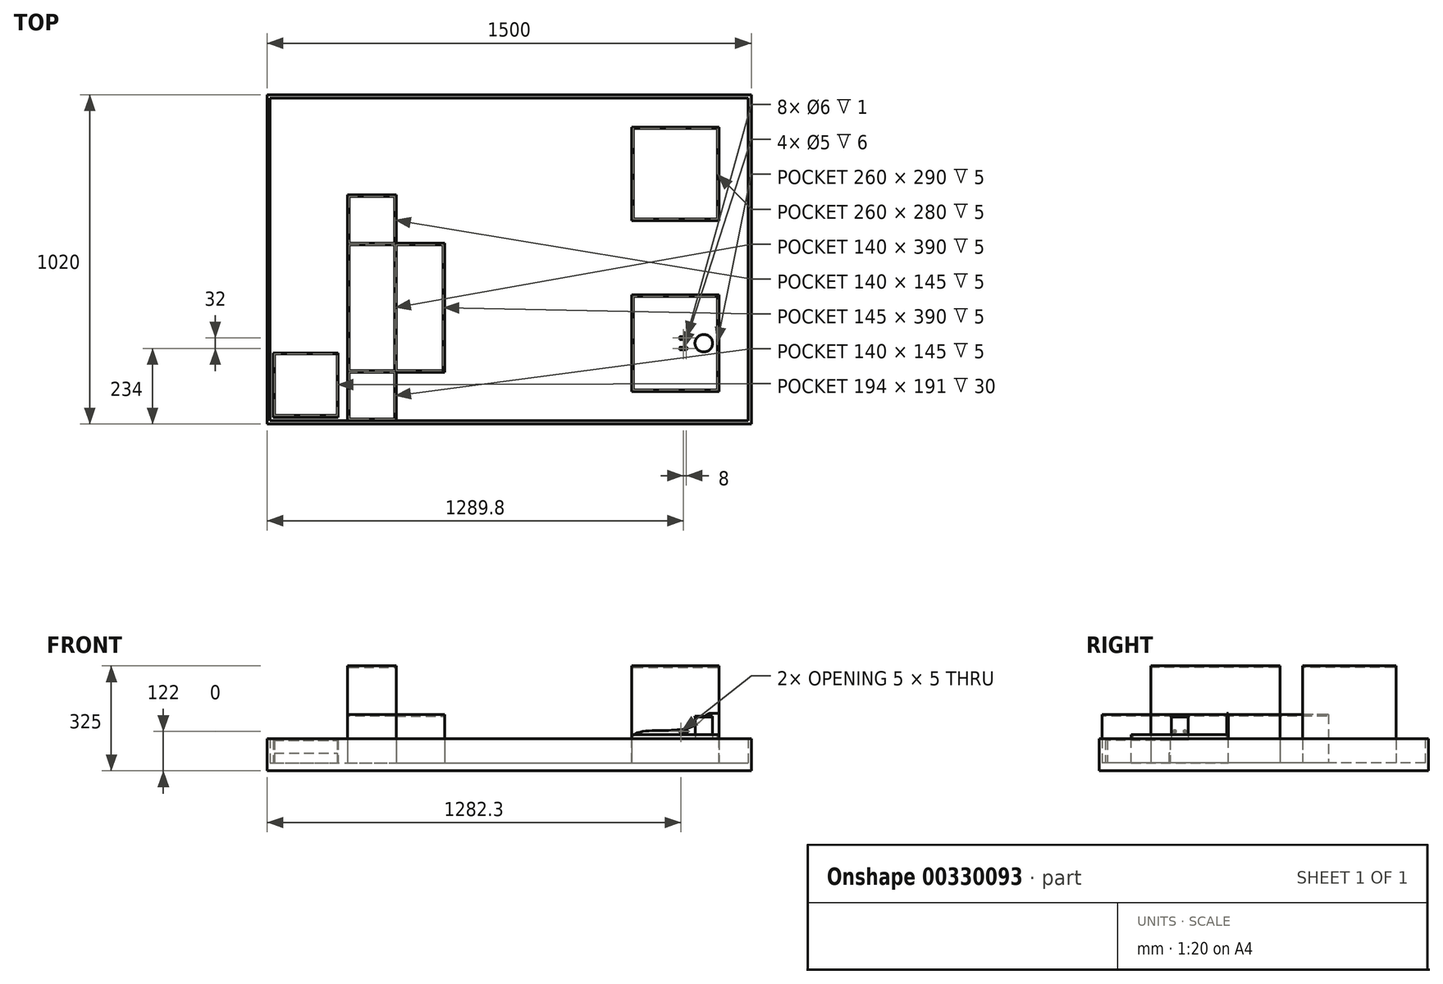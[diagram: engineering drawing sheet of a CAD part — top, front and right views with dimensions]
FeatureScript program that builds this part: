
annotation { "Feature Type Name" : "Feature", "Feature Type Description" : "" }
export const myFeature = defineFeature(function(context is Context, id is Id, definition is map)
    precondition{}
    {
        {
            var Q0;
            Q0=qCreatedBy(makeId("Top.planeOp"),FACE);
            var sketch = newSketch(context, id + "F0", { "sketchPlane" : qUnion([Q0])});
            skCircle(sketch, "E0", {"center": v(0, 0) * mm, "radius": 27.2 * mm});
            skSolve(sketch);
        }
        {
            var Q0;
            Q0=qSketchRegion(id+"F0",true);
            extrude(context, id + "F1", {"entities" : qUnion([Q0]), "depth" : 2.83 * mm});
        }
        {
            var Q0;
            Q0=makeQuery(id+"F1.opExtrude","CAP_FACE",FACE,{"disambiguationData":[OSD([sQuery(id+"F0.wireOp",EDGE,"E0")])],"isStart":false});
            var sketch = newSketch(context, id + "F2", { "sketchPlane" : qUnion([Q0])});
            skCircle(sketch, "E1", {"center": v(0, 0) * mm, "radius": 26.4 * mm});
            skSolve(sketch);
        }
        {
            var Q0;
            Q0=qSketchRegion(id+"F2",true);
            extrude(context, id + "F3", {"entities" : qUnion([Q0]), "operationType" : NewBodyOperationType.ADD, "depth" : 67.36 * mm});
        }
        {
            var Q0;
            Q0=makeQuery(id+"F3.opExtrude","CAP_FACE",FACE,{"disambiguationData":[OSD([sQuery(id+"F2.wireOp",EDGE,"E1")])],"isStart":false});
            var sketch = newSketch(context, id + "F4", { "sketchPlane" : qUnion([Q0])});
            skCircle(sketch, "E2", {"center": v(0, 0) * mm, "radius": 27.2 * mm});
            skSolve(sketch);
        }
        {
            var Q0;
            Q0=qSketchRegion(id+"F4",true);
            extrude(context, id + "F5", {"entities" : qUnion([Q0]), "operationType" : NewBodyOperationType.ADD, "depth" : 2.83 * mm});
        }
        {
            var Q0;
            Q0=makeQuery(id+"F5.opExtrude","CAP_FACE",FACE,{"disambiguationData":[OSD([sQuery(id+"F4.wireOp",EDGE,"E2")])],"isStart":false});
            var sketch = newSketch(context, id + "F6", { "sketchPlane" : qUnion([Q0])});
            skSolve(sketch);
        }
        {
            var Q0;
            Q0=qCreatedBy(makeId("Top.planeOp"),FACE);
            cPlane(context, id + "F7", {"entities" : qUnion([Q0]), "cplaneType" : CPlaneType.OFFSET, "offset" : 25 * mm, "width" : 150 * mm, "height" : 150 * mm});
        }
        {
            var Q0;
            Q0=makeQuery(id+"F6.imprint","IMPRINT",FACE,{"disambiguationData":[TD([[makeQuery(id+"F6.imprint","IMPRINT",EDGE,{"derivedFrom":makeQuery(id+"F5.opExtrude","CAP_EDGE",EDGE,{"disambiguationData":[OSD([sQuery(id+"F4.wireOp",EDGE,"E2")])],"isStart":false})}),1.0]])]});
            var sketch = newSketch(context, id + "F8", { "sketchPlane" : qUnion([Q0])});
            skSolve(sketch);
        }
        {
            var Q0;
            Q0=qCreatedBy(makeId("Top.planeOp"),FACE);
            var sketch = newSketch(context, id + "F9", { "sketchPlane" : qUnion([Q0])});
            skLineSegment(sketch, "E3.bottom", {"start": v(-222.8, -150) * mm, "end": v(47.2, -150) * mm});
            skLineSegment(sketch, "E3.top", {"start": v(-222.8, 150) * mm, "end": v(47.2, 150) * mm});
            skLineSegment(sketch, "E3.left", {"start": v(-222.8, -150) * mm, "end": v(-222.8, 150) * mm});
            skLineSegment(sketch, "E3.right", {"start": v(47.2, -150) * mm, "end": v(47.2, 150) * mm});
            skSolve(sketch);
        }
        {
            var Q0;
            Q0=qSketchRegion(id+"F9",true);
            extrude(context, id + "F10", {"entities" : qUnion([Q0]), "oppositeDirection" : true, "depth" : 72 * mm});
        }
        {
            var Q0;
            Q0=makeQuery(id+"F10.opExtrude","CAP_FACE",FACE,{"disambiguationData":[OSD([sQuery(id+"F9.wireOp",EDGE,"E3.bottom"),sQuery(id+"F9.wireOp",EDGE,"E3.top"),sQuery(id+"F9.wireOp",EDGE,"E3.left"),sQuery(id+"F9.wireOp",EDGE,"E3.right")])],"isStart":true});
            var sketch = newSketch(context, id + "F11", { "sketchPlane" : qUnion([Q0])});
            skLineSegment(sketch, "E4.bottom", {"start": v(-222.8, -150) * mm, "end": v(47.2, -150) * mm});
            skLineSegment(sketch, "E4.top", {"start": v(-222.8, -145) * mm, "end": v(42.2, -145) * mm});
            skLineSegment(sketch, "E4.left", {"start": v(-222.8, -150) * mm, "end": v(-222.8, -145) * mm});
            skLineSegment(sketch, "E5.bottom", {"start": v(47.2, 150) * mm, "end": v(42.2, 150) * mm});
            skLineSegment(sketch, "E5.left", {"start": v(47.2, 150) * mm, "end": v(47.2, -150) * mm});
            skLineSegment(sketch, "E5.right", {"start": v(42.2, 150) * mm, "end": v(42.2, -145) * mm});
            skSolve(sketch);
        }
        {
            var Q0;
            Q0=qSketchRegion(id+"F11",true);
            extrude(context, id + "F12", {"entities" : qUnion([Q0]), "operationType" : NewBodyOperationType.ADD, "depth" : 15 * mm});
        }
        {
            var Q0;
            Q0=makeQuery(id+"F12.boolean.opBoolean","MERGE",FACE,{"derivedFrom":[makeQuery(id+"F10.opExtrude","SWEPT_FACE",FACE,{"disambiguationData":[OSD([sQuery(id+"F9.wireOp",EDGE,"E3.top")])]}),makeQuery(id+"F12.opExtrude","SWEPT_FACE",FACE,{"disambiguationData":[OSD([sQuery(id+"F11.wireOp",EDGE,"E5.bottom")])]})]});
            var sketch = newSketch(context, id + "F13", { "sketchPlane" : qUnion([Q0])});
            skLineSegment(sketch, "E6", {"start": v(-47.2, 81.36) * mm, "end": v(-21.31, 81.36) * mm});
            skFitSpline(sketch, "E7", {"points": [v(-21.31, 81.36) * mm, v(15.24, 52.01) * mm, v(114.14, 28.17) * mm, v(222.8, 0) * mm], "startDerivative": vector(181.02, 0.3) * mm, "endDerivative": vector(-1.73, -239.85) * mm});
            skLineSegment(sketch, "E8", {"start": v(-47.2, 81.36) * mm, "end": v(-47.2, -72) * mm});
            skLineSegment(sketch, "E9", {"start": v(-47.2, -72) * mm, "end": v(222.8, -72) * mm});
            skLineSegment(sketch, "E10", {"start": v(222.8, -72) * mm, "end": v(222.8, 0) * mm});
            skSolve(sketch);
        }
        {
            var Q0;
            Q0=qSketchRegion(id+"F13",true);
            extrude(context, id + "F14", {"entities" : qUnion([Q0]), "operationType" : NewBodyOperationType.ADD, "oppositeDirection" : true, "depth" : 5 * mm});
        }
        {
            var Q0;
            Q0=makeQuery(id+"F10.opExtrude","CAP_FACE",FACE,{"disambiguationData":[OSD([sQuery(id+"F9.wireOp",EDGE,"E3.bottom"),sQuery(id+"F9.wireOp",EDGE,"E3.top"),sQuery(id+"F9.wireOp",EDGE,"E3.left"),sQuery(id+"F9.wireOp",EDGE,"E3.right")])],"isStart":true});
            var sketch = newSketch(context, id + "F15", { "sketchPlane" : qUnion([Q0])});
            skLineSegment(sketch, "E11.bottom", {"start": v(-222.8, 145) * mm, "end": v(-217.8, 145) * mm});
            skLineSegment(sketch, "E11.top", {"start": v(-222.8, -145) * mm, "end": v(-217.8, -145) * mm});
            skLineSegment(sketch, "E11.left", {"start": v(-222.8, 145) * mm, "end": v(-222.8, -145) * mm});
            skLineSegment(sketch, "E11.right", {"start": v(-217.8, 145) * mm, "end": v(-217.8, -145) * mm});
            skSolve(sketch);
        }
        {
            var Q0;
            Q0=qSketchRegion(id+"F15",true);
            extrude(context, id + "F16", {"entities" : qUnion([Q0]), "operationType" : NewBodyOperationType.ADD, "depth" : 5 * mm});
        }
        {
            var Q0;
            Q0=makeQuery(id+"F10.opExtrude","CAP_FACE",FACE,{"disambiguationData":[OSD([sQuery(id+"F9.wireOp",EDGE,"E3.bottom"),sQuery(id+"F9.wireOp",EDGE,"E3.top"),sQuery(id+"F9.wireOp",EDGE,"E3.left"),sQuery(id+"F9.wireOp",EDGE,"E3.right")])],"isStart":false});
            var sketch = newSketch(context, id + "F17", { "sketchPlane" : qUnion([Q0])});
            skLineSegment(sketch, "E12.bottom", {"start": v(147.2, 250) * mm, "end": v(-1352.8, 250) * mm});
            skLineSegment(sketch, "E12.top", {"start": v(147.2, -770) * mm, "end": v(-1352.8, -770) * mm});
            skLineSegment(sketch, "E12.left", {"start": v(147.2, 250) * mm, "end": v(147.2, -770) * mm});
            skLineSegment(sketch, "E12.right", {"start": v(-1352.8, 250) * mm, "end": v(-1352.8, -770) * mm});
            skSolve(sketch);
        }
        {
            var Q0;
            Q0=qSketchRegion(id+"F17",true);
            extrude(context, id + "F18", {"entities" : qUnion([Q0]), "operationType" : NewBodyOperationType.ADD, "depth" : 25 * mm});
        }
        {
            var Q0;
            Q0=makeQuery(id+"F18.opExtrude","CAP_FACE",FACE,{"disambiguationData":[OSD([sQuery(id+"F17.wireOp",EDGE,"E12.bottom"),sQuery(id+"F17.wireOp",EDGE,"E12.top"),sQuery(id+"F17.wireOp",EDGE,"E12.left"),sQuery(id+"F17.wireOp",EDGE,"E12.right")])],"isStart":true});
            var sketch = newSketch(context, id + "F19", { "sketchPlane" : qUnion([Q0])});
            skLineSegment(sketch, "E13.bottom", {"start": v(-222.8, 670) * mm, "end": v(47.2, 670) * mm});
            skLineSegment(sketch, "E13.top", {"start": v(-222.8, 380) * mm, "end": v(47.2, 380) * mm});
            skLineSegment(sketch, "E13.left", {"start": v(-222.8, 670) * mm, "end": v(-222.8, 380) * mm});
            skLineSegment(sketch, "E13.right", {"start": v(47.2, 670) * mm, "end": v(47.2, 380) * mm});
            skSolve(sketch);
        }
        {
            var Q0;
            Q0=qSketchRegion(id+"F19",true);
            extrude(context, id + "F20", {"entities" : qUnion([Q0]), "operationType" : NewBodyOperationType.ADD, "depth" : 300 * mm});
        }
        {
            var Q0;
            Q0=makeQuery(id+"F20.opExtrude","CAP_FACE",FACE,{"disambiguationData":[OSD([sQuery(id+"F19.wireOp",EDGE,"E13.bottom"),sQuery(id+"F19.wireOp",EDGE,"E13.top"),sQuery(id+"F19.wireOp",EDGE,"E13.left"),sQuery(id+"F19.wireOp",EDGE,"E13.right")])],"isStart":false});
            var sketch = newSketch(context, id + "F21", { "sketchPlane" : qUnion([Q0])});
            skLineSegment(sketch, "E14.bottom", {"start": v(-217.8, 665) * mm, "end": v(42.2, 665) * mm});
            skLineSegment(sketch, "E14.top", {"start": v(-217.8, 385) * mm, "end": v(42.2, 385) * mm});
            skLineSegment(sketch, "E14.left", {"start": v(-217.8, 665) * mm, "end": v(-217.8, 385) * mm});
            skLineSegment(sketch, "E14.right", {"start": v(42.2, 665) * mm, "end": v(42.2, 385) * mm});
            skSolve(sketch);
        }
        {
            var Q0;
            Q0=qSketchRegion(id+"F21",true);
            extrude(context, id + "F22", {"entities" : qUnion([Q0]), "operationType" : NewBodyOperationType.REMOVE, "oppositeDirection" : true, "depth" : 5 * mm});
        }
        {
            var Q0;
            Q0=makeQuery(id+"F18.opExtrude","CAP_FACE",FACE,{"disambiguationData":[OSD([sQuery(id+"F17.wireOp",EDGE,"E12.bottom"),sQuery(id+"F17.wireOp",EDGE,"E12.top"),sQuery(id+"F17.wireOp",EDGE,"E12.left"),sQuery(id+"F17.wireOp",EDGE,"E12.right")])],"isStart":true});
            var sketch = newSketch(context, id + "F23", { "sketchPlane" : qUnion([Q0])});
            skLineSegment(sketch, "E15.bottom", {"start": v(-1352.8, 770) * mm, "end": v(147.2, 770) * mm});
            skLineSegment(sketch, "E15.top", {"start": v(-1352.8, -250) * mm, "end": v(147.2, -250) * mm});
            skLineSegment(sketch, "E15.left", {"start": v(-1352.8, 770) * mm, "end": v(-1352.8, -250) * mm});
            skLineSegment(sketch, "E15.right", {"start": v(147.2, 770) * mm, "end": v(147.2, -250) * mm});
            skLineSegment(sketch, "E16.bottom", {"start": v(-1342.8, 760) * mm, "end": v(137.2, 760) * mm});
            skLineSegment(sketch, "E16.top", {"start": v(-1342.8, -240) * mm, "end": v(137.2, -240) * mm});
            skLineSegment(sketch, "E16.left", {"start": v(-1342.8, 760) * mm, "end": v(-1342.8, -240) * mm});
            skLineSegment(sketch, "E16.right", {"start": v(137.2, 760) * mm, "end": v(137.2, -240) * mm});
            skSolve(sketch);
        }
        {
            var Q0;
            Q0=qSketchRegion(id+"F23",true);
            extrude(context, id + "F24", {"entities" : qUnion([Q0]), "operationType" : NewBodyOperationType.ADD, "depth" : 75 * mm});
        }
        {
            var Q0;
            Q0=makeQuery(id+"F18.opExtrude","CAP_FACE",FACE,{"disambiguationData":[OSD([sQuery(id+"F17.wireOp",EDGE,"E12.bottom"),sQuery(id+"F17.wireOp",EDGE,"E12.top"),sQuery(id+"F17.wireOp",EDGE,"E12.left"),sQuery(id+"F17.wireOp",EDGE,"E12.right")])],"isStart":true});
            var sketch = newSketch(context, id + "F25", { "sketchPlane" : qUnion([Q0])});
            skLineSegment(sketch, "E17.bottom", {"start": v(-1102.8, 460) * mm, "end": v(-952.8, 460) * mm});
            skLineSegment(sketch, "E17.top", {"start": v(-1102.8, -240) * mm, "end": v(-952.8, -240) * mm});
            skLineSegment(sketch, "E17.left", {"start": v(-1102.8, 460) * mm, "end": v(-1102.8, -240) * mm});
            skLineSegment(sketch, "E17.right", {"start": v(-952.8, 460) * mm, "end": v(-952.8, 310) * mm});
            skLineSegment(sketch, "E18.bottom", {"start": v(-952.8, 310) * mm, "end": v(-802.8, 310) * mm});
            skLineSegment(sketch, "E18.top", {"start": v(-952.8, -90) * mm, "end": v(-802.8, -90) * mm});
            skLineSegment(sketch, "E18.right", {"start": v(-802.8, 310) * mm, "end": v(-802.8, -90) * mm});
            skLineSegment(sketch, "E19.trimOffspring", {"start": v(-952.8, -90) * mm, "end": v(-952.8, -240) * mm});
            skSolve(sketch);
        }
        {
            var Q0;
            Q0=qSketchRegion(id+"F25",true);
            extrude(context, id + "F26", {"entities" : qUnion([Q0]), "operationType" : NewBodyOperationType.ADD, "depth" : 150 * mm});
        }
        {
            var Q0;
            Q0=makeQuery(id+"F26.opExtrude","CAP_FACE",FACE,{"disambiguationData":[OSD([sQuery(id+"F25.wireOp",EDGE,"E17.bottom"),sQuery(id+"F25.wireOp",EDGE,"E17.top"),sQuery(id+"F25.wireOp",EDGE,"E17.left"),sQuery(id+"F25.wireOp",EDGE,"E17.right"),sQuery(id+"F25.wireOp",EDGE,"E18.bottom"),sQuery(id+"F25.wireOp",EDGE,"E18.top"),sQuery(id+"F25.wireOp",EDGE,"E18.right"),sQuery(id+"F25.wireOp",EDGE,"E19.trimOffspring")])],"isStart":false});
            var sketch = newSketch(context, id + "F27", { "sketchPlane" : qUnion([Q0])});
            skLineSegment(sketch, "E20.bottom", {"start": v(-952.8, 310) * mm, "end": v(-1102.8, 310) * mm});
            skLineSegment(sketch, "E20.top", {"start": v(-952.8, -90) * mm, "end": v(-1102.8, -90) * mm});
            skLineSegment(sketch, "E20.left", {"start": v(-952.8, 310) * mm, "end": v(-952.8, -90) * mm});
            skLineSegment(sketch, "E20.right", {"start": v(-1102.8, 310) * mm, "end": v(-1102.8, -90) * mm});
            skSolve(sketch);
        }
        {
            var Q0;
            Q0=qSketchRegion(id+"F27",true);
            extrude(context, id + "F28", {"entities" : qUnion([Q0]), "operationType" : NewBodyOperationType.ADD, "depth" : 150 * mm});
        }
        {
            var Q0;
            Q0=makeQuery(id+"F28.opExtrude","CAP_FACE",FACE,{"disambiguationData":[OSD([sQuery(id+"F27.wireOp",EDGE,"E20.bottom"),sQuery(id+"F27.wireOp",EDGE,"E20.top"),sQuery(id+"F27.wireOp",EDGE,"E20.left"),sQuery(id+"F27.wireOp",EDGE,"E20.right")])],"isStart":false});
            var sketch = newSketch(context, id + "F29", { "sketchPlane" : qUnion([Q0])});
            skLineSegment(sketch, "E21.bottom", {"start": v(-1097.8, 305) * mm, "end": v(-957.8, 305) * mm});
            skLineSegment(sketch, "E21.top", {"start": v(-1097.8, -85) * mm, "end": v(-957.8, -85) * mm});
            skLineSegment(sketch, "E21.left", {"start": v(-1097.8, 305) * mm, "end": v(-1097.8, -85) * mm});
            skLineSegment(sketch, "E21.right", {"start": v(-957.8, 305) * mm, "end": v(-957.8, -85) * mm});
            skSolve(sketch);
        }
        {
            var Q0;
            Q0=qSketchRegion(id+"F29",true);
            extrude(context, id + "F30", {"entities" : qUnion([Q0]), "operationType" : NewBodyOperationType.REMOVE, "oppositeDirection" : true, "depth" : 5 * mm});
        }
        {
            var Q0;
            {var subQ0=sQuery(id+"F25.wireOp",EDGE,"E17.left");var subQ1=sQuery(id+"F25.wireOp",EDGE,"E18.bottom");var subQ2=sQuery(id+"F25.wireOp",EDGE,"E17.right");var subQ3=sQuery(id+"F25.wireOp",EDGE,"E17.bottom");var subQ4=makeQuery(id+"F26.opExtrude","CAP_FACE",FACE,{"disambiguationData":[OSD([subQ3,sQuery(id+"F25.wireOp",EDGE,"E17.top"),subQ0,subQ2,subQ1,sQuery(id+"F25.wireOp",EDGE,"E18.top"),sQuery(id+"F25.wireOp",EDGE,"E18.right"),sQuery(id+"F25.wireOp",EDGE,"E19.trimOffspring")])],"isStart":false});Q0=makeQuery(id+"F28.boolean.opBoolean","SPLIT",FACE,{"disambiguationData":[TD([makeQuery(id+"F26.opExtrude","SWEPT_FACE",FACE,{"disambiguationData":[OSD([subQ3])]})])],"derivedFrom":subQ4});}
            var sketch = newSketch(context, id + "F31", { "sketchPlane" : qUnion([Q0])});
            skLineSegment(sketch, "E22.bottom", {"start": v(-1097.8, 455) * mm, "end": v(-957.8, 455) * mm});
            skLineSegment(sketch, "E22.top", {"start": v(-1097.8, 310) * mm, "end": v(-957.8, 310) * mm});
            skLineSegment(sketch, "E22.left", {"start": v(-1097.8, 455) * mm, "end": v(-1097.8, 310) * mm});
            skLineSegment(sketch, "E22.right", {"start": v(-957.8, 455) * mm, "end": v(-957.8, 310) * mm});
            skLineSegment(sketch, "E23.bottom", {"start": v(-952.8, 305) * mm, "end": v(-807.8, 305) * mm});
            skLineSegment(sketch, "E23.top", {"start": v(-952.8, -85) * mm, "end": v(-807.8, -85) * mm});
            skLineSegment(sketch, "E23.left", {"start": v(-952.8, 305) * mm, "end": v(-952.8, -85) * mm});
            skLineSegment(sketch, "E23.right", {"start": v(-807.8, 305) * mm, "end": v(-807.8, -85) * mm});
            skLineSegment(sketch, "E24.bottom", {"start": v(-1097.8, -90) * mm, "end": v(-957.8, -90) * mm});
            skLineSegment(sketch, "E24.top", {"start": v(-1097.8, -235) * mm, "end": v(-957.8, -235) * mm});
            skLineSegment(sketch, "E24.left", {"start": v(-1097.8, -90) * mm, "end": v(-1097.8, -235) * mm});
            skLineSegment(sketch, "E24.right", {"start": v(-957.8, -90) * mm, "end": v(-957.8, -235) * mm});
            skSolve(sketch);
        }
        {
            var Q0;
            Q0=qSketchRegion(id+"F31",true);
            extrude(context, id + "F32", {"entities" : qUnion([Q0]), "operationType" : NewBodyOperationType.REMOVE, "oppositeDirection" : true, "depth" : 5 * mm});
        }
        {
            var Q0;
            Q0=qCreatedBy(id+"F7.planeOp",FACE);
            var sketch = newSketch(context, id + "F33", { "sketchPlane" : qUnion([Q0])});
            skLineSegment(sketch, "E25", {"start": v(0, 0) * mm, "end": v(-90, 0) * mm, "construction": true});
            skLineSegment(sketch, "E26.bottom", {"start": v(-74.5, -12) * mm, "end": v(-55, -12) * mm});
            skLineSegment(sketch, "E26.top", {"start": v(-74.5, -20) * mm, "end": v(-55, -20) * mm});
            skLineSegment(sketch, "E26.left", {"start": v(-74.5, -12) * mm, "end": v(-74.5, -13) * mm});
            skPoint(sketch, "E27.visualSharp", {"position": v(-51, -12) * mm});
            skPoint(sketch, "E28.visualSharp", {"position": v(-51, -20) * mm});
            skCircle(sketch, "E29", {"center": v(-55, -16) * mm, "radius": 3 * mm});
            skLineSegment(sketch, "E30", {"start": v(-59, -3.98) * mm, "end": v(-59, -18.08) * mm, "construction": true});
            skCircle(sketch, "E31.MirrorC", {"center": v(-63, -16) * mm, "radius": 3 * mm});
            skLineSegment(sketch, "E32.bottom", {"start": v(-74.5, -13) * mm, "end": v(-65.65, -13) * mm});
            skLineSegment(sketch, "E32.top", {"start": v(-74.5, -19) * mm, "end": v(-65.65, -19) * mm});
            skArc(sketch, "E33", {"start": v(-65.65, -13) * mm, "mid": v(-67, -16) * mm, "end": v(-65.65, -19) * mm});
            skLineSegment(sketch, "E34.trimOffspring", {"start": v(-74.5, -19) * mm, "end": v(-74.5, -20) * mm});
            skArc(sketch, "E35.trimOffspring", {"start": v(-55, -20) * mm, "mid": v(-51, -16) * mm, "end": v(-55, -12) * mm});
            skLineSegment(sketch, "E36.MirrorCS", {"start": v(-74.5, 12) * mm, "end": v(-74.5, 13) * mm});
            skLineSegment(sketch, "E37.MirrorCS", {"start": v(-74.5, 19) * mm, "end": v(-74.5, 20) * mm});
            skPoint(sketch, "E38.MirrorP", {"position": v(-51, 12) * mm});
            skLineSegment(sketch, "E39.MirrorCS", {"start": v(-74.5, 12) * mm, "end": v(-55, 12) * mm});
            skPoint(sketch, "E40.MirrorP", {"position": v(-51, 20) * mm});
            skArc(sketch, "E41.MirrorCS", {"start": v(-65.65, 13) * mm, "mid": v(-67, 16) * mm, "end": v(-65.65, 19) * mm});
            skArc(sketch, "E42.MirrorCS", {"start": v(-55, 20) * mm, "mid": v(-51, 16) * mm, "end": v(-55, 12) * mm});
            skLineSegment(sketch, "E43.MirrorCS", {"start": v(-74.5, 20) * mm, "end": v(-55, 20) * mm});
            skCircle(sketch, "E44.MirrorC", {"center": v(-55, 16) * mm, "radius": 3 * mm});
            skCircle(sketch, "E45.MirrorC", {"center": v(-63, 16) * mm, "radius": 3 * mm});
            skLineSegment(sketch, "E46.MirrorCS", {"start": v(-74.5, 19) * mm, "end": v(-65.65, 19) * mm});
            skLineSegment(sketch, "E47.MirrorCS", {"start": v(-74.5, 13) * mm, "end": v(-65.65, 13) * mm});
            skSolve(sketch);
        }
        {
            var Q0;
            Q0=qSketchRegion(id+"F33",true);
            var Q1;
            Q1=qSketchRegion(id+"F36",true);
            extrude(context, id + "F34", {"entities" : qUnion([Q0, Q1]), "endBound" : BoundingType.SYMMETRIC, "depth" : 8 * mm});
        }
        {
            var Q0;
            Q0=makeQuery(id+"F34.opExtrude","CAP_EDGE",EDGE,{"disambiguationData":[OSD([sQuery(id+"F33.wireOp",EDGE,"E34.trimOffspring")])],"isStart":false});
            var Q1;
            Q1=makeQuery(id+"F34.opExtrude","CAP_EDGE",EDGE,{"disambiguationData":[OSD([sQuery(id+"F33.wireOp",EDGE,"E26.left")])],"isStart":false});
            var Q2;
            Q2=makeQuery(id+"F34.opExtrude","CAP_EDGE",EDGE,{"disambiguationData":[OSD([sQuery(id+"F33.wireOp",EDGE,"E34.trimOffspring")])],"isStart":true});
            var Q3;
            Q3=makeQuery(id+"F34.opExtrude","CAP_EDGE",EDGE,{"disambiguationData":[OSD([sQuery(id+"F33.wireOp",EDGE,"E26.left")])],"isStart":true});
            var Q4;
            Q4=makeQuery(id+"F34.opExtrude","CAP_EDGE",EDGE,{"disambiguationData":[OSD([sQuery(id+"F33.wireOp",EDGE,"E36.MirrorCS")])],"isStart":false});
            var Q5;
            Q5=makeQuery(id+"F34.opExtrude","CAP_EDGE",EDGE,{"disambiguationData":[OSD([sQuery(id+"F33.wireOp",EDGE,"E37.MirrorCS")])],"isStart":false});
            var Q6;
            Q6=makeQuery(id+"F34.opExtrude","CAP_EDGE",EDGE,{"disambiguationData":[OSD([sQuery(id+"F33.wireOp",EDGE,"E37.MirrorCS")])],"isStart":true});
            var Q7;
            Q7=makeQuery(id+"F34.opExtrude","CAP_EDGE",EDGE,{"disambiguationData":[OSD([sQuery(id+"F33.wireOp",EDGE,"E36.MirrorCS")])],"isStart":true});
            fillet(context, id + "F35", {"entities" : qUnion([Q0, Q1, Q2, Q3, Q4, Q5, Q6, Q7]), "radius" : 4 * mm, "tangentPropagation" : true, "allowEdgeOverflow" : false});
        }
        {
            var Q0;
            Q0=makeQuery(id+"F34.opExtrude","SWEPT_FACE",FACE,{"disambiguationData":[OSD([sQuery(id+"F33.wireOp",EDGE,"E26.top")])]});
            var sketch = newSketch(context, id + "F36", { "sketchPlane" : qUnion([Q0])});
            skCircle(sketch, "E48", {"center": v(-70.5, 25) * mm, "radius": 3 * mm});
            skSolve(sketch);
        }
        {
            var Q0;
            Q0=qSketchRegion(id+"F36",true);
            var Q1;
            Q1=makeQuery(id+"F34.opExtrude","SWEPT_FACE",FACE,{"disambiguationData":[OSD([sQuery(id+"F33.wireOp",EDGE,"E26.bottom")])]});
            extrude(context, id + "F37", {"entities" : qUnion([Q0]), "operationType" : NewBodyOperationType.ADD, "endBound" : BoundingType.UP_TO_SURFACE, "oppositeDirection" : true, "endBoundEntityFace" : qUnion([Q1]), "depth" : 25 * mm});
        }
        {
            var Q0;
            Q0=makeQuery(id+"F34.opExtrude","SWEPT_FACE",FACE,{"disambiguationData":[OSD([sQuery(id+"F33.wireOp",EDGE,"E43.MirrorCS")])]});
            var sketch = newSketch(context, id + "F38", { "sketchPlane" : qUnion([Q0])});
            skCircle(sketch, "E49", {"center": v(70.5, 25) * mm, "radius": 3 * mm});
            skSolve(sketch);
        }
        {
            var Q0;
            Q0=qSketchRegion(id+"F38",true);
            var Q1;
            Q1=makeQuery(id+"F34.opExtrude","SWEPT_FACE",FACE,{"disambiguationData":[OSD([sQuery(id+"F33.wireOp",EDGE,"E39.MirrorCS")])]});
            extrude(context, id + "F39", {"entities" : qUnion([Q0]), "operationType" : NewBodyOperationType.ADD, "endBound" : BoundingType.UP_TO_SURFACE, "oppositeDirection" : true, "endBoundEntityFace" : qUnion([Q1]), "depth" : 25 * mm});
        }
        {
            var Q0;
            Q0=qCreatedBy(id+"F7.planeOp",FACE);
            var sketch = newSketch(context, id + "F40", { "sketchPlane" : qUnion([Q0])});
            skCircle(sketch, "E50", {"center": v(-55, 16) * mm, "radius": 3 * mm});
            skCircle(sketch, "E51", {"center": v(-63, 16) * mm, "radius": 2.5 * mm});
            skCircle(sketch, "E52", {"center": v(-63, 16) * mm, "radius": 3 * mm});
            skCircle(sketch, "E53", {"center": v(-55, 16) * mm, "radius": 2.5 * mm});
            skSolve(sketch);
        }
        {
            var Q0;
            Q0=qSketchRegion(id+"F40",true);
            extrude(context, id + "F41", {"entities" : qUnion([Q0]), "operationType" : NewBodyOperationType.ADD, "endBound" : BoundingType.SYMMETRIC, "depth" : 6 * mm});
        }
        {
            var Q0;
            Q0=qCreatedBy(id+"F7.planeOp",FACE);
            var sketch = newSketch(context, id + "F42", { "sketchPlane" : qUnion([Q0])});
            skCircle(sketch, "E54", {"center": v(-63, -16) * mm, "radius": 2.5 * mm});
            skCircle(sketch, "E55", {"center": v(-63, -16) * mm, "radius": 3 * mm});
            skCircle(sketch, "E56", {"center": v(-55, -16) * mm, "radius": 2.5 * mm});
            skCircle(sketch, "E57", {"center": v(-55, -16) * mm, "radius": 3 * mm});
            skSolve(sketch);
        }
        {
            var Q0;
            Q0=qSketchRegion(id+"F42",true);
            extrude(context, id + "F43", {"entities" : qUnion([Q0]), "operationType" : NewBodyOperationType.ADD, "endBound" : BoundingType.SYMMETRIC, "depth" : 6 * mm});
        }
        {
            var Q0;
            Q0=makeQuery(id+"F34.opExtrude","SWEPT_FACE",FACE,{"disambiguationData":[OSD([sQuery(id+"F33.wireOp",EDGE,"E43.MirrorCS")])]});
            var sketch = newSketch(context, id + "F44", { "sketchPlane" : qUnion([Q0])});
            skArc(sketch, "E58", {"start": v(71.5, 27.3) * mm, "mid": v(70.5, 27.5) * mm, "end": v(69.5, 27.3) * mm});
            skLineSegment(sketch, "E59.bottom", {"start": v(68.2, 26) * mm, "end": v(69.5, 26) * mm});
            skLineSegment(sketch, "E59.top", {"start": v(68.2, 24) * mm, "end": v(69.5, 24) * mm});
            skLineSegment(sketch, "E60.left", {"start": v(71.5, 27.3) * mm, "end": v(71.5, 26) * mm});
            skLineSegment(sketch, "E60.right", {"start": v(69.5, 27.3) * mm, "end": v(69.5, 26) * mm});
            skPoint(sketch, "E61.orphan", {"position": v(69.5, 27.8) * mm});
            skPoint(sketch, "E62.orphan", {"position": v(71.5, 27.8) * mm});
            skArc(sketch, "E63.trimOffspring", {"start": v(68.2, 26) * mm, "mid": v(68, 25) * mm, "end": v(68.2, 24) * mm});
            skPoint(sketch, "E59.left.start.orphan", {"position": v(67.32, 26) * mm});
            skPoint(sketch, "E64.orphan", {"position": v(67.32, 24) * mm});
            skArc(sketch, "E65.trimOffspring", {"start": v(69.5, 22.7) * mm, "mid": v(70.5, 22.5) * mm, "end": v(71.5, 22.7) * mm});
            skLineSegment(sketch, "E66.trimOffspring", {"start": v(69.5, 24) * mm, "end": v(69.5, 22.7) * mm});
            skLineSegment(sketch, "E67.trimOffspring", {"start": v(71.5, 26) * mm, "end": v(72.8, 26) * mm});
            skLineSegment(sketch, "E68.trimOffspring", {"start": v(71.5, 24) * mm, "end": v(71.5, 22.7) * mm});
            skLineSegment(sketch, "E69.trimOffspring", {"start": v(71.5, 24) * mm, "end": v(72.8, 24) * mm});
            skPoint(sketch, "E60.top.end.orphan", {"position": v(69.5, 22.2) * mm});
            skPoint(sketch, "E70.orphan", {"position": v(71.5, 22.2) * mm});
            skPoint(sketch, "E59.right.end.orphan", {"position": v(73.68, 24) * mm});
            skPoint(sketch, "E71.orphan", {"position": v(73.68, 26) * mm});
            skArc(sketch, "E72.trimOffspring", {"start": v(72.8, 24) * mm, "mid": v(73, 25) * mm, "end": v(72.8, 26) * mm});
            skSolve(sketch);
        }
        {
            var Q0;
            Q0=qSketchRegion(id+"F44",true);
            extrude(context, id + "F45", {"entities" : qUnion([Q0]), "operationType" : NewBodyOperationType.REMOVE, "endBound" : BoundingType.THROUGH_ALL, "oppositeDirection" : true, "depth" : 25 * mm});
        }
        {
            var Q0;
            Q0=makeQuery(id+"F18.opExtrude","CAP_FACE",FACE,{"disambiguationData":[OSD([sQuery(id+"F17.wireOp",EDGE,"E12.bottom"),sQuery(id+"F17.wireOp",EDGE,"E12.top"),sQuery(id+"F17.wireOp",EDGE,"E12.left"),sQuery(id+"F17.wireOp",EDGE,"E12.right")])],"isStart":true});
            var sketch = newSketch(context, id + "F46", { "sketchPlane" : qUnion([Q0])});
            skLineSegment(sketch, "E73.bottom", {"start": v(-1332.8, -30) * mm, "end": v(-1132.8, -30) * mm});
            skLineSegment(sketch, "E73.top", {"start": v(-1332.8, -230) * mm, "end": v(-1132.8, -230) * mm});
            skLineSegment(sketch, "E73.left", {"start": v(-1332.8, -30) * mm, "end": v(-1332.8, -230) * mm});
            skLineSegment(sketch, "E73.right", {"start": v(-1132.8, -30) * mm, "end": v(-1132.8, -230) * mm});
            skLineSegment(sketch, "E74.bottom", {"start": v(-1329.8, -33) * mm, "end": v(-1135.8, -33) * mm});
            skLineSegment(sketch, "E74.top", {"start": v(-1329.8, -224) * mm, "end": v(-1135.8, -224) * mm});
            skLineSegment(sketch, "E74.left", {"start": v(-1329.8, -33) * mm, "end": v(-1329.8, -224) * mm});
            skLineSegment(sketch, "E74.right", {"start": v(-1135.8, -33) * mm, "end": v(-1135.8, -224) * mm});
            skSolve(sketch);
        }
        {
            var Q0;
            Q0=qSketchRegion(id+"F46",true);
            extrude(context, id + "F47", {"entities" : qUnion([Q0]), "operationType" : NewBodyOperationType.ADD, "depth" : 30 * mm});
        }
        {
            var Q0;
            Q0=makeQuery(id+"F47.opExtrude","CAP_FACE",FACE,{"disambiguationData":[OSD([sQuery(id+"F46.wireOp",EDGE,"E73.bottom"),sQuery(id+"F46.wireOp",EDGE,"E73.top"),sQuery(id+"F46.wireOp",EDGE,"E73.left"),sQuery(id+"F46.wireOp",EDGE,"E73.right"),sQuery(id+"F46.wireOp",EDGE,"E74.bottom"),sQuery(id+"F46.wireOp",EDGE,"E74.top"),sQuery(id+"F46.wireOp",EDGE,"E74.left"),sQuery(id+"F46.wireOp",EDGE,"E74.right")])],"isStart":false});
            var sketch = newSketch(context, id + "F48", { "sketchPlane" : qUnion([Q0])});
            skLineSegment(sketch, "E75.bottom", {"start": v(-1332.8, -30) * mm, "end": v(-1329.8, -30) * mm});
            skLineSegment(sketch, "E75.top", {"start": v(-1332.8, -230) * mm, "end": v(-1329.8, -230) * mm});
            skLineSegment(sketch, "E75.left", {"start": v(-1332.8, -30) * mm, "end": v(-1332.8, -230) * mm});
            skLineSegment(sketch, "E75.right", {"start": v(-1329.8, -30) * mm, "end": v(-1329.8, -224) * mm});
            skLineSegment(sketch, "E76.bottom", {"start": v(-1329.8, -230) * mm, "end": v(-1135.8, -230) * mm});
            skLineSegment(sketch, "E76.top", {"start": v(-1329.8, -224) * mm, "end": v(-1135.8, -224) * mm});
            skLineSegment(sketch, "E77.bottom", {"start": v(-1135.8, -230) * mm, "end": v(-1132.8, -230) * mm});
            skLineSegment(sketch, "E77.top", {"start": v(-1135.8, -30) * mm, "end": v(-1132.8, -30) * mm});
            skLineSegment(sketch, "E77.left", {"start": v(-1135.8, -224) * mm, "end": v(-1135.8, -30) * mm});
            skLineSegment(sketch, "E77.right", {"start": v(-1132.8, -230) * mm, "end": v(-1132.8, -30) * mm});
            skSolve(sketch);
        }
        {
            var Q0;
            Q0=qSketchRegion(id+"F48",true);
            extrude(context, id + "F49", {"entities" : qUnion([Q0]), "operationType" : NewBodyOperationType.ADD, "depth" : 40 * mm});
        }
    });
